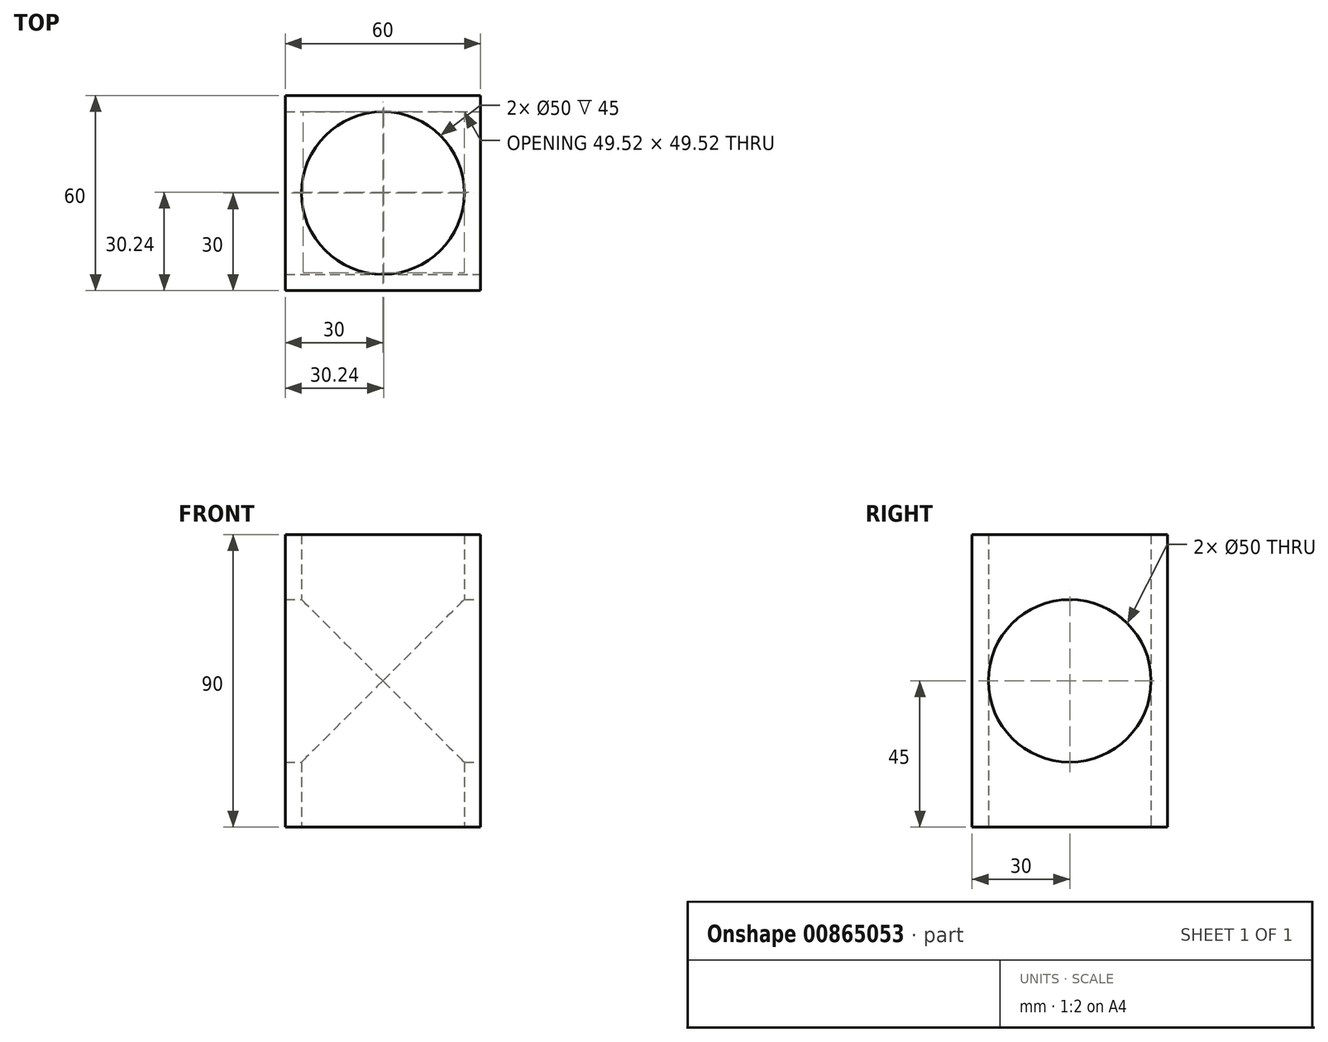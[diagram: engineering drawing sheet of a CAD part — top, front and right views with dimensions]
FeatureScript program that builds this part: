
annotation { "Feature Type Name" : "Feature", "Feature Type Description" : "" }
export const myFeature = defineFeature(function(context is Context, id is Id, definition is map)
    precondition{}
    {
        {
            var Q0;
            Q0=qCreatedBy(makeId("Top.planeOp"),FACE);
            var sketch = newSketch(context, id + "F0", { "sketchPlane" : qUnion([Q0])});
            skLineSegment(sketch, "E0.bottom", {"start": v(30, -30) * mm, "end": v(-30, -30) * mm});
            skLineSegment(sketch, "E0.top", {"start": v(30, 30) * mm, "end": v(-30, 30) * mm});
            skLineSegment(sketch, "E0.left", {"start": v(30, -30) * mm, "end": v(30, 30) * mm});
            skLineSegment(sketch, "E0.right", {"start": v(-30, -30) * mm, "end": v(-30, 30) * mm});
            skPoint(sketch, "E0.middle", {"position": v(0, 0) * mm});
            skCircle(sketch, "E1", {"center": v(0, 0) * mm, "radius": 25 * mm});
            skLineSegment(sketch, "E2", {"start": v(0, 0) * mm, "end": v(-30, 30) * mm, "construction": true});
            skLineSegment(sketch, "E3", {"start": v(0, 25) * mm, "end": v(-30, 25) * mm, "construction": true});
            skPoint(sketch, "E3.startSnap0", {"position": v(0, 30) * mm});
            skSolve(sketch);
        }
        {
            var Q0;
            Q0 = qSketchRegion(id + "F0", true);
            extrude(context, id + "F1", {"entities" : qUnion([Q0]), "endBound" : BoundingType.SYMMETRIC, "depth" : 90 * mm, "offsetDistance" : 25 * mm});
        }
        {
            var Q0;
            Q0=makeQuery(id+"F1.opExtrude","SWEPT_FACE",FACE,{"disambiguationData":[OSD([sQuery(id+"F0.wireOp",EDGE,"E0.left")])]});
            var sketch = newSketch(context, id + "F2", { "sketchPlane" : qUnion([Q0])});
            skCircle(sketch, "E4", {"center": v(0, 0) * mm, "radius": 25 * mm});
            skSolve(sketch);
        }
        {
            var Q0;
            Q0 = qSketchRegion(id + "F2", true);
            extrude(context, id + "F3", {"entities" : qUnion([Q0]), "operationType" : NewBodyOperationType.REMOVE, "endBound" : BoundingType.THROUGH_ALL, "oppositeDirection" : true, "depth" : 25 * mm, "offsetDistance" : 25 * mm});
        }
    });
